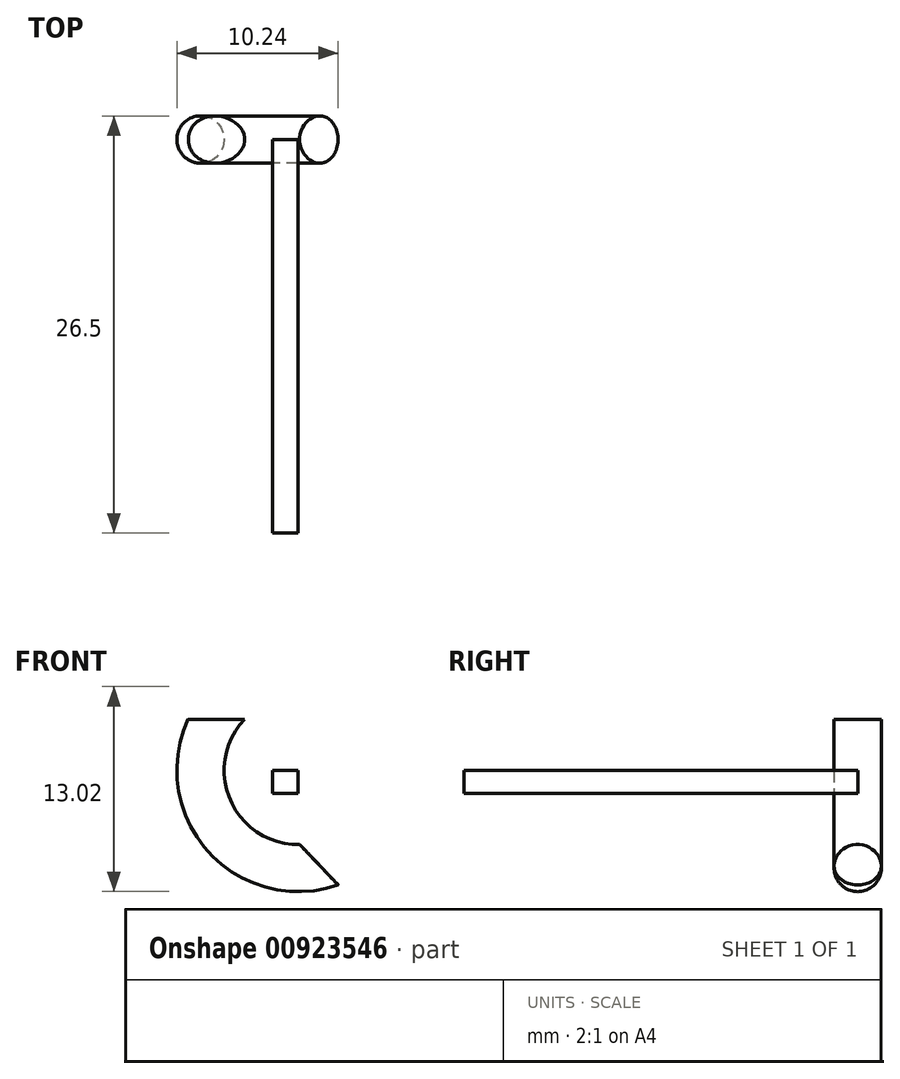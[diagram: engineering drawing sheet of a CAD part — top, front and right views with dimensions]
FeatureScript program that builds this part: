
annotation { "Feature Type Name" : "Feature", "Feature Type Description" : "" }
export const myFeature = defineFeature(function(context is Context, id is Id, definition is map)
    precondition{}
    {
        {
            var Q0;
            Q0=qCreatedBy(makeId("Front.planeOp"),FACE);
            var sketch = newSketch(context, id + "F0", { "sketchPlane" : qUnion([Q0])});
            skLineSegment(sketch, "E0.bottom", {"start": v(-12.15, -1.44) * mm, "end": v(-13.77, -1.44) * mm});
            skLineSegment(sketch, "E0.top", {"start": v(-12.15, -2.9) * mm, "end": v(-13.77, -2.9) * mm});
            skLineSegment(sketch, "E0.left", {"start": v(-12.15, -1.44) * mm, "end": v(-12.15, -2.9) * mm});
            skLineSegment(sketch, "E0.right", {"start": v(-13.77, -1.44) * mm, "end": v(-13.77, -2.9) * mm});
            skSolve(sketch);
        }
        {
            var Q0;
            Q0=makeQuery(id+"F0.imprint","IMPRINT",FACE,{"disambiguationData":[TD([[makeQuery(id+"F0.imprint","IMPRINT",EDGE,{"derivedFrom":sQuery(id+"F0.wireOp",EDGE,"E0.bottom")}),1.0]])]});
            extrude(context, id + "F1", {"entities" : qUnion([Q0]), "depth" : 25 * mm, "offsetDistance" : 25 * mm});
        }
        {
            var Q0;
            Q0=makeQuery(id+"F1.opExtrude","SWEPT_FACE",FACE,{"disambiguationData":[OSD([sQuery(id+"F0.wireOp",EDGE,"E0.left")])]});
            var sketch = newSketch(context, id + "F2", { "sketchPlane" : qUnion([Q0])});
            skCircle(sketch, "E1", {"center": v(0, -7.64) * mm, "radius": 1.5 * mm});
            skSolve(sketch);
        }
        {
            var Q0;
            Q0=makeQuery(id+"F2.imprint","IMPRINT",FACE,{"disambiguationData":[TD([[makeQuery(id+"F2.imprint","IMPRINT",EDGE,{"derivedFrom":sQuery(id+"F2.wireOp",EDGE,"E1")}),1.0]])]});
            var Q1;
            Q1=makeQuery(id+"F1.opExtrude","SWEPT_EDGE",EDGE,{"disambiguationData":[OSD([sQuery(id+"F0.wireOp",EDGE,"E0.bottom"),sQuery(id+"F0.wireOp",EDGE,"E0.left")])]});
            revolve(context, id + "F3", {"surfaceOperationType" : NewSurfaceOperationType.NEW, "entities" : qUnion([Q0]), "axis" : qUnion([Q1]), "revolveType" : RevolveType.FULL});
        }
        {
            var Q0;
            Q0=qCreatedBy(makeId("Front.planeOp"),FACE);
            var sketch = newSketch(context, id + "F4", { "sketchPlane" : qUnion([Q0])});
            skLineSegment(sketch, "E2.bottom", {"start": v(2.9, 17.57) * mm, "end": v(-26.85, 17.57) * mm});
            skLineSegment(sketch, "E2.top", {"start": v(2.9, 1.81) * mm, "end": v(-26.85, 1.81) * mm});
            skLineSegment(sketch, "E2.left", {"start": v(2.9, 17.57) * mm, "end": v(2.9, 1.81) * mm});
            skLineSegment(sketch, "E2.right", {"start": v(-26.85, 17.57) * mm, "end": v(-26.85, 1.81) * mm});
            skSolve(sketch);
        }
        {
            var Q0;
            Q0=makeQuery(id+"F4.imprint","IMPRINT",FACE,{"disambiguationData":[TD([[makeQuery(id+"F4.imprint","IMPRINT",EDGE,{"derivedFrom":sQuery(id+"F4.wireOp",EDGE,"E2.bottom")}),1.0]])]});
            extrude(context, id + "F5", {"entities" : qUnion([Q0]), "operationType" : NewBodyOperationType.REMOVE, "endBound" : BoundingType.SYMMETRIC, "depth" : 25 * mm, "offsetDistance" : 25 * mm});
        }
        {
            var Q0;
            Q0=makeQuery(id+"F0.imprint","IMPRINT",FACE,{"disambiguationData":[TD([[makeQuery(id+"F0.imprint","IMPRINT",EDGE,{"derivedFrom":sQuery(id+"F0.wireOp",EDGE,"E0.bottom")}),1.0]])]});
            var sketch = newSketch(context, id + "F6", { "sketchPlane" : qUnion([Q0])});
            skLineSegment(sketch, "E3", {"start": v(-11.69, 3.23) * mm, "end": v(-12.17, -6.02) * mm});
            skLineSegment(sketch, "E4", {"start": v(-12.17, -6.02) * mm, "end": v(-5.75, -12.78) * mm});
            skLineSegment(sketch, "E5", {"start": v(-5.75, -12.78) * mm, "end": v(3.6, 5.62) * mm});
            skLineSegment(sketch, "E6", {"start": v(3.6, 5.62) * mm, "end": v(-11.69, 3.23) * mm});
            skSolve(sketch);
        }
        {
            var Q0;
            Q0=makeQuery(id+"F6.imprint","IMPRINT",FACE,{"disambiguationData":[TD([[makeQuery(id+"F6.imprint","IMPRINT",EDGE,{"derivedFrom":sQuery(id+"F6.wireOp",EDGE,"E3")}),1.0]])]});
            extrude(context, id + "F7", {"entities" : qUnion([Q0]), "operationType" : NewBodyOperationType.REMOVE, "endBound" : BoundingType.SYMMETRIC, "oppositeDirection" : true, "depth" : 25 * mm, "offsetDistance" : 25 * mm});
        }
    });
